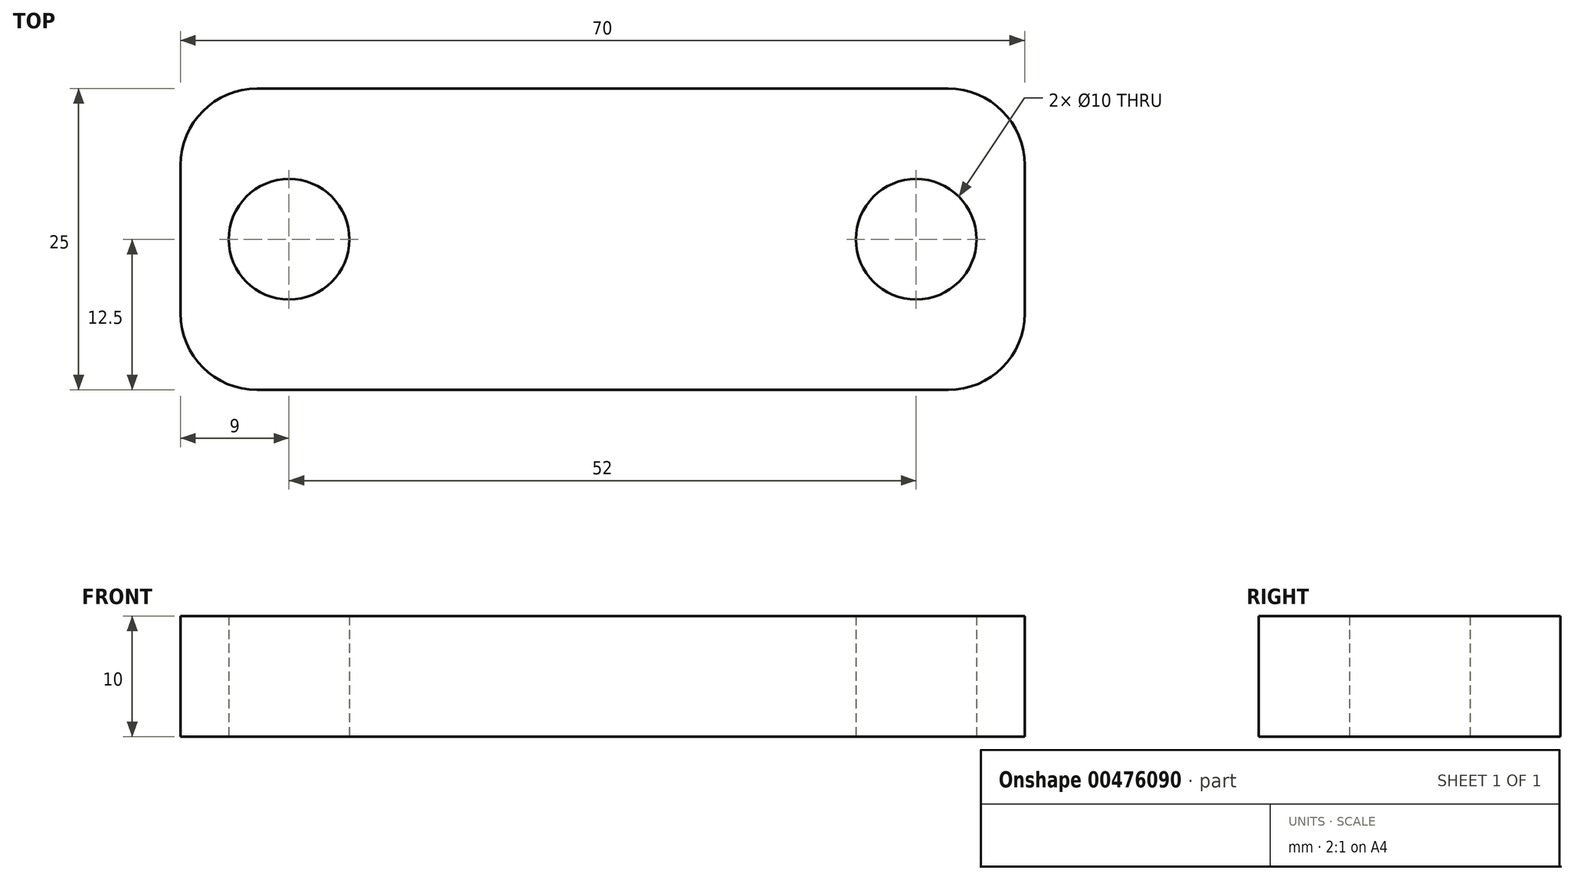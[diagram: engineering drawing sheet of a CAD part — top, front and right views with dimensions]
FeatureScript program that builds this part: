
annotation { "Feature Type Name" : "Feature", "Feature Type Description" : "" }
export const myFeature = defineFeature(function(context is Context, id is Id, definition is map)
    precondition{}
    {
        {
            var Q0;
            Q0=qCreatedBy(makeId("Top.planeOp"),FACE);
            cPlane(context, id + "F0", {"entities" : qUnion([Q0]), "cplaneType" : CPlaneType.OFFSET, "offset" : 25.4 * mm, "width" : 152.4 * mm, "height" : 152.4 * mm});
        }
        {
            var Q0;
            Q0=qCreatedBy(id+"F0.planeOp",FACE);
            var sketch = newSketch(context, id + "F1", { "sketchPlane" : qUnion([Q0])});
            skLineSegment(sketch, "E0.bottom", {"start": v(35, -12.5) * mm, "end": v(-35, -12.5) * mm});
            skLineSegment(sketch, "E0.top", {"start": v(35, 12.5) * mm, "end": v(-35, 12.5) * mm});
            skLineSegment(sketch, "E0.left", {"start": v(35, -12.5) * mm, "end": v(35, 12.5) * mm});
            skLineSegment(sketch, "E0.right", {"start": v(-35, -12.5) * mm, "end": v(-35, 12.5) * mm});
            skPoint(sketch, "E0.middle", {"position": v(0, 0) * mm});
            skCircle(sketch, "E1", {"center": v(-26, 0) * mm, "radius": 5 * mm});
            skCircle(sketch, "E2.MirrorC", {"center": v(26, 0) * mm, "radius": 5 * mm});
            skSolve(sketch);
        }
        {
            var Q0;
            Q0=makeQuery(id+"F1.imprint","IMPRINT",FACE,{"disambiguationData":[TD([[makeQuery(id+"F1.imprint","IMPRINT",EDGE,{"derivedFrom":sQuery(id+"F1.wireOp",EDGE,"E0.bottom")}),-1.0]])]});
            extrude(context, id + "F2", {"entities" : qUnion([Q0]), "depth" : 10 * mm});
        }
        {
            var Q0;
            Q0=makeQuery(id+"F2.opExtrude","SWEPT_EDGE",EDGE,{"disambiguationData":[OSD([sQuery(id+"F1.wireOp",EDGE,"E0.top"),sQuery(id+"F1.wireOp",EDGE,"E0.right")])]});
            var Q1;
            Q1=makeQuery(id+"F2.opExtrude","SWEPT_EDGE",EDGE,{"disambiguationData":[OSD([sQuery(id+"F1.wireOp",EDGE,"E0.top"),sQuery(id+"F1.wireOp",EDGE,"E0.left")])]});
            var Q2;
            Q2=makeQuery(id+"F2.opExtrude","SWEPT_EDGE",EDGE,{"disambiguationData":[OSD([sQuery(id+"F1.wireOp",EDGE,"E0.bottom"),sQuery(id+"F1.wireOp",EDGE,"E0.left")])]});
            var Q3;
            Q3=makeQuery(id+"F2.opExtrude","SWEPT_EDGE",EDGE,{"disambiguationData":[OSD([sQuery(id+"F1.wireOp",EDGE,"E0.bottom"),sQuery(id+"F1.wireOp",EDGE,"E0.right")])]});
            fillet(context, id + "F3", {"entities" : qUnion([Q0, Q1, Q2, Q3]), "radius" : 6.35 * mm, "tangentPropagation" : true, "allowEdgeOverflow" : false});
        }
    });
